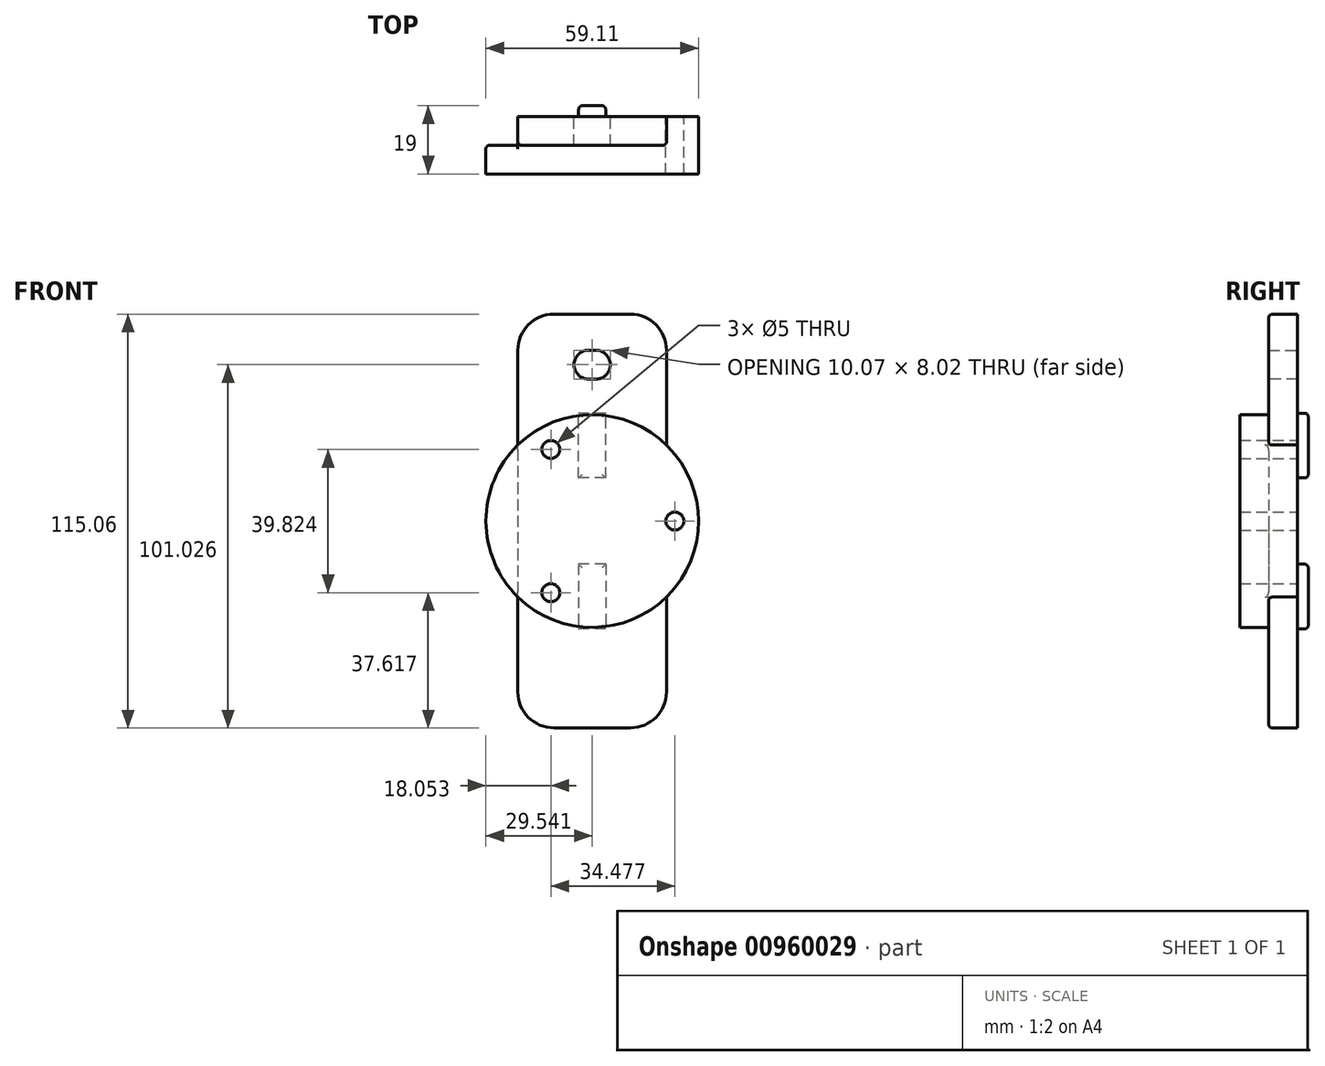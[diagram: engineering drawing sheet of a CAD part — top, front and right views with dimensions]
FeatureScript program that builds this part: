
annotation { "Feature Type Name" : "Feature", "Feature Type Description" : "" }
export const myFeature = defineFeature(function(context is Context, id is Id, definition is map)
    precondition{}
    {
        {
            var Q0;
            Q0=qCreatedBy(makeId("Front.planeOp"),FACE);
            var sketch = newSketch(context, id + "F0", { "sketchPlane" : qUnion([Q0])});
            skLineSegment(sketch, "E0.bottom", {"start": v(-20.66, 57.53) * mm, "end": v(20.66, 57.53) * mm});
            skLineSegment(sketch, "E0.top", {"start": v(-20.66, -57.53) * mm, "end": v(20.66, -57.53) * mm});
            skLineSegment(sketch, "E0.left", {"start": v(-20.66, 57.53) * mm, "end": v(-20.66, -57.53) * mm});
            skLineSegment(sketch, "E0.right", {"start": v(20.66, 57.53) * mm, "end": v(20.66, -57.53) * mm});
            skPoint(sketch, "E0.middle", {"position": v(0, 0) * mm});
            skSolve(sketch);
        }
        {
            var Q0;
            Q0 = qSketchRegion(id + "F0", true);
            extrude(context, id + "F1", {"entities" : qUnion([Q0]), "depth" : 8 * mm, "offsetDistance" : 25.4 * mm});
        }
        {
            var Q0;
            Q0=makeQuery(id+"F0.imprint","IMPRINT",FACE,{"disambiguationData":[TD([[makeQuery(id+"F0.imprint","IMPRINT",EDGE,{"derivedFrom":sQuery(id+"F0.wireOp",EDGE,"E0.bottom")}),-1.0]])]});
            var sketch = newSketch(context, id + "F2", { "sketchPlane" : qUnion([Q0])});
            skCircle(sketch, "E1", {"center": v(0, 0) * mm, "radius": 29.57 * mm});
            skPoint(sketch, "E2", {"position": v(23, 0) * mm});
            skPoint(sketch, "E3", {"position": v(-11.49, 19.91) * mm});
            skPoint(sketch, "E4", {"position": v(-11.49, -19.91) * mm});
            skSolve(sketch);
        }
        {
            var Q0;
            {var subQ0=sQuery(id+"F2.wireOp",EDGE,"E1");var subQ1=makeQuery(id+"F0.imprint","IMPRINT",EDGE,{"derivedFrom":sQuery(id+"F0.wireOp",EDGE,"E0.left")});var subQ2=makeQuery(id+"F2.imprint","INTERSECT",VERTEX,{"disambiguationData":[OD(0.0)],"derivedFrom":[subQ1,subQ0]});Q0=makeQuery(id+"F2.imprint","IMPRINT",FACE,{"disambiguationData":[TD([[makeQuery(id+"F2.imprint","IMPRINT",EDGE,{"disambiguationData":[TD([[subQ2,1.0]])],"derivedFrom":subQ0}),1.0]])]});}
            var Q1;
            {var subQ0=sQuery(id+"F2.wireOp",EDGE,"E1");var subQ1=makeQuery(id+"F0.imprint","IMPRINT",EDGE,{"derivedFrom":sQuery(id+"F0.wireOp",EDGE,"E0.right")});var subQ2=makeQuery(id+"F2.imprint","INTERSECT",VERTEX,{"disambiguationData":[OD(0.0)],"derivedFrom":[subQ1,subQ0]});Q1=makeQuery(id+"F2.imprint","IMPRINT",FACE,{"disambiguationData":[TD([[makeQuery(id+"F2.imprint","IMPRINT",EDGE,{"disambiguationData":[TD([[subQ2,1.0]])],"derivedFrom":subQ0}),1.0]])]});}
            var Q2;
            Q2=sQuery(id+"F2.wireOp",EDGE,"E1");
            extrude(context, id + "F3", {"entities" : qUnion([Q0, Q1]), "surfaceEntities" : qUnion([Q2]), "depth" : 16 * mm, "offsetDistance" : 25.4 * mm});
        }
        {
            var Q0;
            Q0=makeQuery(id+"F1.opExtrude","CAP_FACE",FACE,{"disambiguationData":[OSD([sQuery(id+"F0.wireOp",EDGE,"E0.bottom"),sQuery(id+"F0.wireOp",EDGE,"E0.top"),sQuery(id+"F0.wireOp",EDGE,"E0.left"),sQuery(id+"F0.wireOp",EDGE,"E0.right")])],"isStart":true});
            var sketch = newSketch(context, id + "F4", { "sketchPlane" : qUnion([Q0])});
            skLineSegment(sketch, "E5", {"start": v(5.04, 47.5) * mm, "end": v(5.04, 39.49) * mm});
            skLineSegment(sketch, "E6", {"start": v(-5.04, 39.48) * mm, "end": v(-5.04, 47.5) * mm});
            skLineSegment(sketch, "E7", {"start": v(5.04, 39.49) * mm, "end": v(-5.04, 39.48) * mm});
            skLineSegment(sketch, "E8", {"start": v(-5.04, 47.5) * mm, "end": v(5.04, 47.5) * mm});
            skSolve(sketch);
        }
        {
            var Q0;
            Q0 = qSketchRegion(id + "F4", true);
            extrude(context, id + "F5", {"entities" : qUnion([Q0]), "operationType" : NewBodyOperationType.REMOVE, "oppositeDirection" : true, "depth" : 8.5 * mm, "offsetDistance" : 25.4 * mm});
        }
        {
            var Q0;
            Q0=makeQuery(id+"F5.boolean.opBoolean","COPY",EDGE,{"derivedFrom":makeQuery(id+"F5.opExtrude","SWEPT_EDGE",EDGE,{"disambiguationData":[OSD([sQuery(id+"F4.wireOp",EDGE,"E6"),sQuery(id+"F4.wireOp",EDGE,"VEhSB0G0-dWcA-gG2V-vMXn-voc8N2IHvjFB")])]})});
            var Q1;
            Q1=makeQuery(id+"F5.boolean.opBoolean","COPY",EDGE,{"derivedFrom":makeQuery(id+"F5.opExtrude","SWEPT_EDGE",EDGE,{"disambiguationData":[OSD([sQuery(id+"F4.wireOp",EDGE,"XE8fgab3-rSFt-7oTP-HbAQ-i8VjvcFRi00H"),sQuery(id+"F4.wireOp",EDGE,"E5")])]})});
            var Q2;
            Q2=makeQuery(id+"F5.boolean.opBoolean","COPY",EDGE,{"derivedFrom":makeQuery(id+"F5.opExtrude","SWEPT_EDGE",EDGE,{"disambiguationData":[OSD([sQuery(id+"F4.wireOp",EDGE,"E5"),sQuery(id+"F4.wireOp",EDGE,"8kUsppU3-GCa5-UIFq-wueu-n7haDhcSVEqN")])]})});
            var Q3;
            Q3=makeQuery(id+"F5.boolean.opBoolean","COPY",EDGE,{"derivedFrom":makeQuery(id+"F5.opExtrude","SWEPT_EDGE",EDGE,{"disambiguationData":[OSD([sQuery(id+"F4.wireOp",EDGE,"ImzeJQY2-ZgP6-6dGd-gt1C-XoDUwymdjZeL"),sQuery(id+"F4.wireOp",EDGE,"E6")])]})});
            fillet(context, id + "F6", {"entities" : qUnion([Q0, Q1, Q2, Q3]), "radius" : 4 * mm, "tangentPropagation" : true, "allowEdgeOverflow" : false});
        }
        {
            var Q0;
            Q0=makeQuery(id+"F1.opExtrude","SWEPT_EDGE",EDGE,{"disambiguationData":[OSD([sQuery(id+"F0.wireOp",EDGE,"E0.bottom"),sQuery(id+"F0.wireOp",EDGE,"E0.right")])]});
            var Q1;
            Q1=makeQuery(id+"F1.opExtrude","SWEPT_EDGE",EDGE,{"disambiguationData":[OSD([sQuery(id+"F0.wireOp",EDGE,"E0.bottom"),sQuery(id+"F0.wireOp",EDGE,"E0.left")])]});
            var Q2;
            Q2=makeQuery(id+"F1.opExtrude","SWEPT_EDGE",EDGE,{"disambiguationData":[OSD([sQuery(id+"F0.wireOp",EDGE,"E0.top"),sQuery(id+"F0.wireOp",EDGE,"E0.left")])]});
            var Q3;
            Q3=makeQuery(id+"F1.opExtrude","SWEPT_EDGE",EDGE,{"disambiguationData":[OSD([sQuery(id+"F0.wireOp",EDGE,"E0.top"),sQuery(id+"F0.wireOp",EDGE,"E0.right")])]});
            fillet(context, id + "F7", {"entities" : qUnion([Q0, Q1, Q2, Q3]), "radius" : 10 * mm, "tangentPropagation" : true, "allowEdgeOverflow" : false});
        }
        {
            var Q0;
            Q0=makeQuery(id+"F1.opExtrude","SWEPT_BODY",BODY,{"disambiguationData":[OSD([sQuery(id+"F0.wireOp",EDGE,"E0.bottom"),sQuery(id+"F0.wireOp",EDGE,"E0.top"),sQuery(id+"F0.wireOp",EDGE,"E0.left"),sQuery(id+"F0.wireOp",EDGE,"E0.right")])]});
            var Q1;
            Q1=makeQuery(id+"F3.opExtrude","SWEPT_BODY",BODY,{"disambiguationData":[OSD([sQuery(id+"F2.wireOp",EDGE,"E1")])]});
            booleanBodies(context, id + "F8", {"operationType" : BooleanOperationType.UNION, "tools" : qUnion([Q0, Q1])});
        }
        {
            var Q0;
            Q0=sQuery(id+"F2.wireOp",VERTEX,"E2");
            var Q1;
            Q1=sQuery(id+"F2.wireOp",VERTEX,"E3");
            var Q2;
            Q2=sQuery(id+"F2.wireOp",VERTEX,"E4");
            var Q3;
            Q3=makeQuery(id+"F1.opExtrude","SWEPT_BODY",BODY,{"disambiguationData":[OSD([sQuery(id+"F0.wireOp",EDGE,"E0.bottom"),sQuery(id+"F0.wireOp",EDGE,"E0.top"),sQuery(id+"F0.wireOp",EDGE,"E0.left"),sQuery(id+"F0.wireOp",EDGE,"E0.right")])]});
            hole(context, id + "F9", {"style" : HoleStyle.SIMPLE, "endStyle" : HoleEndStyle.THROUGH, "oppositeDirection" : true, "standardTappedOrClearance" : lookupTablePath({ "standard" : "ISO", "engagement" : "75%", "pitch" : "1 mm", "size" : "M6", "type" : "Tapped" }), "standardBlindInLast" : lookupTablePath({ "standard" : "ISO", "fit" : "Normal", "engagement" : "75%", "pitch" : "1 mm", "size" : "M6", "type" : "Clearance & tapped" }), "holeDiameter" : 5 * mm, "majorDiameter" : 6 * mm, "showTappedDepth" : true, "isTappedThrough" : true, "tappedDepth" : 12.7 * mm, "tapClearance" : 3, "locations" : qUnion([Q0, Q1, Q2]), "scope" : qUnion([Q3])});
        }
        {
            var Q0;
            {var subQ0=sQuery(id+"F0.wireOp",EDGE,"E0.left");var subQ1=sQuery(id+"F0.wireOp",EDGE,"E0.bottom");Q0=makeQuery(id+"F8.opBoolean","SPLIT",EDGE,{"disambiguationData":[TD([makeQuery(id+"F7.opFillet","BLEND_FACE",FACE,{"disambiguationData":[OSD([subQ1,subQ0])]})])],"derivedFrom":makeQuery(id+"F1.opExtrude","CAP_EDGE",EDGE,{"disambiguationData":[OSD([subQ0])],"isStart":false})});}
            var Q1;
            {var subQ0=sQuery(id+"F0.wireOp",EDGE,"E0.left");var subQ1=sQuery(id+"F0.wireOp",EDGE,"E0.top");Q1=makeQuery(id+"F8.opBoolean","SPLIT",EDGE,{"disambiguationData":[TD([makeQuery(id+"F7.opFillet","BLEND_FACE",FACE,{"disambiguationData":[OSD([subQ1,subQ0])]})])],"derivedFrom":makeQuery(id+"F1.opExtrude","CAP_EDGE",EDGE,{"disambiguationData":[OSD([subQ0])],"isStart":false})});}
            fillet(context, id + "F10", {"entities" : qUnion([Q0, Q1]), "radius" : 1 * mm, "tangentPropagation" : true, "allowEdgeOverflow" : false});
        }
        {
            var Q0;
            Q0=makeQuery(id+"F3.opExtrude","CAP_FACE",FACE,{"disambiguationData":[OSD([sQuery(id+"F0.wireOp",EDGE,"E0.left"),sQuery(id+"F2.wireOp",EDGE,"E1")])],"isStart":false});
            var sketch = newSketch(context, id + "F11", { "sketchPlane" : qUnion([Q0])});
            skArc(sketch, "E9", {"start": v(-29.54, 0) * mm, "mid": v(-27.21, -11.46) * mm, "end": v(-20.66, -21.15) * mm});
            skArc(sketch, "E10", {"start": v(-20.66, 21.15) * mm, "mid": v(-27.24, 11.47) * mm, "end": v(-29.54, 0) * mm});
            skLineSegment(sketch, "E11", {"start": v(-20.66, 21.15) * mm, "end": v(-20.66, -21.15) * mm});
            skSolve(sketch);
        }
        {
            var Q0;
            Q0=makeQuery(id+"F11.imprint","IMPRINT",FACE,{"disambiguationData":[TD([[makeQuery(id+"F11.imprint","IMPRINT",EDGE,{"derivedFrom":sQuery(id+"F11.wireOp",EDGE,"E9")}),1.0]])]});
            extrude(context, id + "F12", {"entities" : qUnion([Q0]), "operationType" : NewBodyOperationType.ADD, "oppositeDirection" : true, "depth" : 8 * mm, "offsetDistance" : 25.4 * mm});
        }
        {
            var Q0;
            Q0=makeQuery(id+"F12.opExtrude","CAP_EDGE",EDGE,{"disambiguationData":[OSD([sQuery(id+"F11.wireOp",EDGE,"E10")])],"isStart":false});
            var Q1;
            Q1=makeQuery(id+"F12.opExtrude","CAP_EDGE",EDGE,{"disambiguationData":[OSD([sQuery(id+"F11.wireOp",EDGE,"E9")])],"isStart":false});
            fillet(context, id + "F13", {"entities" : qUnion([Q0, Q1]), "radius" : 1 * mm, "tangentPropagation" : true, "allowEdgeOverflow" : false});
        }
        {
            var Q0;
            Q0=makeQuery(id+"F4.imprint","IMPRINT",FACE,{"disambiguationData":[TD([[makeQuery(id+"F4.imprint","IMPRINT",EDGE,{"derivedFrom":sQuery(id+"F4.wireOp",EDGE,"E5")}),1.0]])]});
            var sketch = newSketch(context, id + "F14", { "sketchPlane" : qUnion([Q0])});
            skLineSegment(sketch, "E12.bottom", {"start": v(-3.75, -12) * mm, "end": v(3.75, -12) * mm});
            skLineSegment(sketch, "E12.top", {"start": v(-3.75, -30) * mm, "end": v(3.75, -30) * mm});
            skLineSegment(sketch, "E12.left", {"start": v(-3.75, -12) * mm, "end": v(-3.75, -30) * mm});
            skLineSegment(sketch, "E12.right", {"start": v(3.75, -12) * mm, "end": v(3.75, -30) * mm});
            skPoint(sketch, "E12.middle", {"position": v(0, -21) * mm});
            skLineSegment(sketch, "E13.bottom", {"start": v(-3.75, 12) * mm, "end": v(3.75, 12) * mm});
            skLineSegment(sketch, "E13.top", {"start": v(-3.75, 30) * mm, "end": v(3.75, 30) * mm});
            skLineSegment(sketch, "E13.left", {"start": v(-3.75, 12) * mm, "end": v(-3.75, 30) * mm});
            skLineSegment(sketch, "E13.right", {"start": v(3.75, 12) * mm, "end": v(3.75, 30) * mm});
            skPoint(sketch, "E13.middle", {"position": v(0, 21) * mm});
            skSolve(sketch);
        }
        {
            var Q0;
            Q0 = qSketchRegion(id + "F14", true);
            extrude(context, id + "F15", {"entities" : qUnion([Q0]), "operationType" : NewBodyOperationType.ADD, "depth" : 3 * mm, "offsetDistance" : 25 * mm});
        }
        {
            var Q0;
            Q0=makeQuery(id+"F15.opExtrude","CAP_FACE",FACE,{"disambiguationData":[OSD([sQuery(id+"F14.wireOp",EDGE,"E13.bottom"),sQuery(id+"F14.wireOp",EDGE,"E13.top"),sQuery(id+"F14.wireOp",EDGE,"E13.left"),sQuery(id+"F14.wireOp",EDGE,"E13.right")])],"isStart":false});
            var Q1;
            Q1=makeQuery(id+"F15.opExtrude","CAP_FACE",FACE,{"disambiguationData":[OSD([sQuery(id+"F14.wireOp",EDGE,"E12.bottom"),sQuery(id+"F14.wireOp",EDGE,"E12.top"),sQuery(id+"F14.wireOp",EDGE,"E12.left"),sQuery(id+"F14.wireOp",EDGE,"E12.right")])],"isStart":false});
            fillet(context, id + "F16", {"entities" : qUnion([Q0, Q1]), "radius" : 1 * mm, "tangentPropagation" : true, "allowEdgeOverflow" : false});
        }
    });
